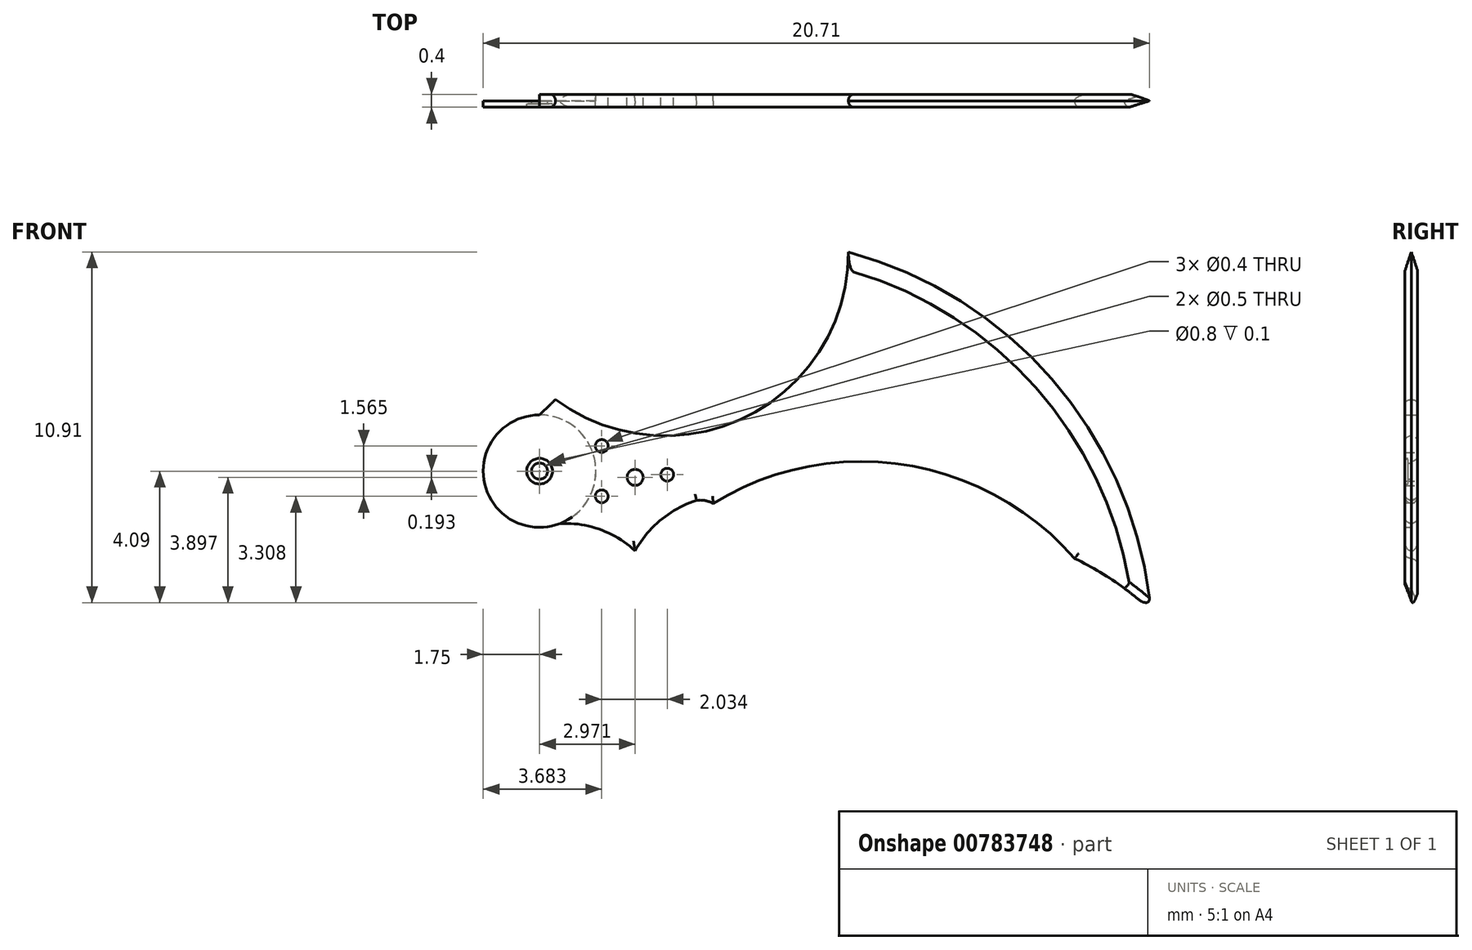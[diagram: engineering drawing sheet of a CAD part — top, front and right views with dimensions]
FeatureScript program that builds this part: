
annotation { "Feature Type Name" : "Feature", "Feature Type Description" : "" }
export const myFeature = defineFeature(function(context is Context, id is Id, definition is map)
    precondition{}
    {
        {
            var Q0;
            Q0=qCreatedBy(makeId("Front.planeOp"),FACE);
            var sketch = newSketch(context, id + "F0", { "sketchPlane" : qUnion([Q0])});
            skPoint(sketch, "E0", {"position": v(12.4, 0) * mm});
            skPoint(sketch, "E1", {"position": v(10, 3) * mm});
            skPoint(sketch, "E2", {"position": v(5.9, 7.4) * mm});
            skPoint(sketch, "E3", {"position": v(0.8, 6.7) * mm});
            skPoint(sketch, "E4", {"position": v(5, 9.8) * mm});
            skPoint(sketch, "E5", {"position": v(0, 11.5) * mm});
            skPoint(sketch, "E6", {"position": v(3.9, 18.3) * mm});
            skPoint(sketch, "E7", {"position": v(6.3, 6) * mm});
            skArc(sketch, "E8", {"start": v(2.97, 9.02) * mm, "mid": v(1.89, 9.68) * mm, "end": v(0.64, 9.87) * mm});
            skCircle(sketch, "E9", {"center": v(0, 11.5) * mm, "radius": 1.75 * mm});
            skArc(sketch, "E10", {"start": v(0.5, 13.73) * mm, "mid": v(6.46, 13.2) * mm, "end": v(9.6, 18.32) * mm});
            skArc(sketch, "E11", {"start": v(5.4, 10.5) * mm, "mid": v(5.14, 10.59) * mm, "end": v(4.88, 10.6) * mm});
            skArc(sketch, "E12", {"start": v(5.83, 10.75) * mm, "mid": v(4.17, 10.27) * mm, "end": v(2.97, 9.02) * mm});
            skArc(sketch, "E13", {"start": v(19, 7.18) * mm, "mid": v(16.04, 14.22) * mm, "end": v(9.6, 18.32) * mm});
            skArc(sketch, "E14", {"start": v(16.63, 8.78) * mm, "mid": v(11.33, 11.7) * mm, "end": v(5.4, 10.5) * mm});
            skArc(sketch, "E15.trimOffspring", {"start": v(19, 7.18) * mm, "mid": v(17.87, 8.07) * mm, "end": v(16.63, 8.78) * mm});
            skLineSegment(sketch, "E16", {"start": v(0, 13.25) * mm, "end": v(0.5, 13.73) * mm});
            skCircle(sketch, "E17", {"center": v(1.93, 12.28) * mm, "radius": 0.2 * mm});
            skLineSegment(sketch, "E18", {"start": v(0, 11.5) * mm, "end": v(5.59, 11.5) * mm, "construction": true});
            skCircle(sketch, "E19", {"center": v(2.97, 11.3) * mm, "radius": 0.25 * mm});
            skCircle(sketch, "E20", {"center": v(3.97, 11.39) * mm, "radius": 0.2 * mm});
            skCircle(sketch, "E21.MirrorC", {"center": v(1.93, 10.72) * mm, "radius": 0.2 * mm});
            skLineSegment(sketch, "E22", {"start": v(0, 15.23) * mm, "end": v(0, 8.3) * mm, "construction": true});
            skCircle(sketch, "E23", {"center": v(0, 11.5) * mm, "radius": 0.25 * mm});
            skCircle(sketch, "E24", {"center": v(0, 11.5) * mm, "radius": 0.4 * mm});
            skSolve(sketch);
        }
        {
            var Q0;
            {var subQ4=sQuery(id+"F0.wireOp",EDGE,"E8");Q0=makeQuery(id+"F0.imprint","IMPRINT",FACE,{"disambiguationData":[TD([[makeQuery(id+"F0.imprint","IMPRINT",EDGE,{"derivedFrom":subQ4}),-1.0]])]});}
            var Q1;
            {var subQ0=sQuery(id+"F0.wireOp",EDGE,"E14");var subQ1=sQuery(id+"F0.wireOp",EDGE,"E11");var subQ2=makeQuery(id+"F0.imprint","INTERSECT",VERTEX,{"derivedFrom":[subQ1,subQ0]});Q1=makeQuery(id+"F0.imprint","IMPRINT",FACE,{"disambiguationData":[TD([[makeQuery(id+"F0.imprint","IMPRINT",EDGE,{"disambiguationData":[TD([[subQ2,-1.0]])],"derivedFrom":subQ1}),-1.0]])]});}
            extrude(context, id + "F1", {"entities" : qUnion([Q0, Q1]), "endBound" : BoundingType.SYMMETRIC, "depth" : .4 * mm, "offsetDistance" : 25 * mm});
        }
        {
            var Q0;
            {var subQ0=sQuery(id+"F0.wireOp",EDGE,"E9");var subQ1=makeQuery(id+"F0.imprint","INTERSECT",VERTEX,{"derivedFrom":[sQuery(id+"F0.wireOp",EDGE,"E8"),subQ0]});Q0=makeQuery(id+"F0.imprint","IMPRINT",FACE,{"disambiguationData":[TD([[makeQuery(id+"F0.imprint","IMPRINT",EDGE,{"disambiguationData":[TD([[subQ1,1.0]])],"derivedFrom":subQ0}),1.0]])]});}
            extrude(context, id + "F2", {"entities" : qUnion([Q0]), "operationType" : NewBodyOperationType.ADD, "depth" : .2 * mm, "offsetDistance" : 25 * mm});
        }
        {
            var Q0;
            Q0=makeQuery(id+"F1.opExtrude","CAP_EDGE",EDGE,{"disambiguationData":[OSD([sQuery(id+"F0.wireOp",EDGE,"E13")])],"isStart":false});
            var Q1;
            Q1=makeQuery(id+"F1.opExtrude","CAP_EDGE",EDGE,{"disambiguationData":[OSD([sQuery(id+"F0.wireOp",EDGE,"E13")])],"isStart":true});
            chamfer(context, id + "F3", {"entities" : qUnion([Q0, Q1]), "chamferType" : ChamferType.OFFSET_ANGLE, "width" : .55 * mm, "oppositeDirection" : false, "angle" : 20 * degree, "tangentPropagation" : true});
        }
        {
            var Q0;
            Q0=makeQuery(id+"F1.opExtrude","CAP_EDGE",EDGE,{"disambiguationData":[OSD([sQuery(id+"F0.wireOp",EDGE,"E10")])],"isStart":false});
            var Q1;
            Q1=makeQuery(id+"F1.opExtrude","CAP_EDGE",EDGE,{"disambiguationData":[OSD([sQuery(id+"F0.wireOp",EDGE,"E14")])],"isStart":false});
            var Q2;
            {var subQ0=sQuery(id+"F0.wireOp",EDGE,"E12");Q2=makeQuery(id+"F1.opExtrude","CAP_EDGE",EDGE,{"disambiguationData":[OSD([subQ0]),TDD([makeQuery(id+"F0.imprint","IMPRINT",EDGE,{"disambiguationData":[TD([[makeQuery(id+"F0.imprint","INTERSECT",VERTEX,{"derivedFrom":[subQ0,sQuery(id+"F0.wireOp",EDGE,"E14")]}),-1.0]])],"derivedFrom":subQ0})])],"isStart":false});}
            var Q3;
            {var subQ0=sQuery(id+"F0.wireOp",EDGE,"E12");Q3=makeQuery(id+"F1.opExtrude","CAP_EDGE",EDGE,{"disambiguationData":[OSD([subQ0]),TDD([makeQuery(id+"F0.imprint","IMPRINT",EDGE,{"disambiguationData":[TD([[makeQuery(id+"F0.imprint","INTERSECT",VERTEX,{"derivedFrom":[sQuery(id+"F0.wireOp",EDGE,"E8"),subQ0]}),1.0]])],"derivedFrom":subQ0})])],"isStart":false});}
            var Q4;
            Q4=makeQuery(id+"F1.opExtrude","CAP_EDGE",EDGE,{"disambiguationData":[OSD([sQuery(id+"F0.wireOp",EDGE,"E11")])],"isStart":false});
            var Q5;
            {var subQ0=sQuery(id+"F0.wireOp",EDGE,"E12");Q5=makeQuery(id+"F1.opExtrude","CAP_EDGE",EDGE,{"disambiguationData":[OSD([subQ0]),TDD([makeQuery(id+"F0.imprint","IMPRINT",EDGE,{"disambiguationData":[TD([[makeQuery(id+"F0.imprint","INTERSECT",VERTEX,{"derivedFrom":[sQuery(id+"F0.wireOp",EDGE,"E8"),subQ0]}),1.0]])],"derivedFrom":subQ0})])],"isStart":true});}
            var Q6;
            {var subQ0=sQuery(id+"F0.wireOp",EDGE,"E12");Q6=makeQuery(id+"F1.opExtrude","CAP_EDGE",EDGE,{"disambiguationData":[OSD([subQ0]),TDD([makeQuery(id+"F0.imprint","IMPRINT",EDGE,{"disambiguationData":[TD([[makeQuery(id+"F0.imprint","INTERSECT",VERTEX,{"derivedFrom":[subQ0,sQuery(id+"F0.wireOp",EDGE,"E14")]}),-1.0]])],"derivedFrom":subQ0})])],"isStart":true});}
            var Q7;
            Q7=makeQuery(id+"F1.opExtrude","CAP_EDGE",EDGE,{"disambiguationData":[OSD([sQuery(id+"F0.wireOp",EDGE,"E11")])],"isStart":true});
            var Q8;
            Q8=makeQuery(id+"F1.opExtrude","CAP_EDGE",EDGE,{"disambiguationData":[OSD([sQuery(id+"F0.wireOp",EDGE,"E14")])],"isStart":true});
            var Q9;
            Q9=makeQuery(id+"F1.opExtrude","CAP_EDGE",EDGE,{"disambiguationData":[OSD([sQuery(id+"F0.wireOp",EDGE,"E8")])],"isStart":true});
            var Q10;
            Q10=makeQuery(id+"F1.opExtrude","CAP_EDGE",EDGE,{"disambiguationData":[OSD([sQuery(id+"F0.wireOp",EDGE,"E8")])],"isStart":false});
            var Q11;
            Q11=makeQuery(id+"F1.opExtrude","CAP_EDGE",EDGE,{"disambiguationData":[OSD([sQuery(id+"F0.wireOp",EDGE,"E10")])],"isStart":true});
            var Q12;
            Q12=makeQuery(id+"F1.opExtrude","CAP_EDGE",EDGE,{"disambiguationData":[OSD([sQuery(id+"F0.wireOp",EDGE,"E15.trimOffspring")])],"isStart":false});
            var Q13;
            Q13=makeQuery(id+"F3.opChamfer","BLEND_EDGE",EDGE,{"blendedFrom":[makeQuery(id+"F1.opExtrude","CAP_EDGE",EDGE,{"disambiguationData":[OSD([sQuery(id+"F0.wireOp",EDGE,"E13")])],"isStart":false}),makeQuery(id+"F1.opExtrude","SWEPT_FACE",FACE,{"disambiguationData":[OSD([sQuery(id+"F0.wireOp",EDGE,"E15.trimOffspring")])]})],"blendedInto":[makeQuery(id+"F1.opExtrude","SWEPT_FACE",FACE,{"disambiguationData":[OSD([sQuery(id+"F0.wireOp",EDGE,"E15.trimOffspring")])]})]});
            fillet(context, id + "F4", {"entities" : qUnion([Q0, Q1, Q2, Q3, Q4, Q5, Q6, Q7, Q8, Q9, Q10, Q11, Q12, Q13]), "radius" : .2 * mm, "tangentPropagation" : true, "allowEdgeOverflow" : false});
        }
        {
            var Q0;
            Q0=makeQuery(id+"F0.imprint","IMPRINT",FACE,{"disambiguationData":[TD([[makeQuery(id+"F0.imprint","IMPRINT",EDGE,{"derivedFrom":sQuery(id+"F0.wireOp",EDGE,"E23")}),-1.0]])]});
            extrude(context, id + "F5", {"entities" : qUnion([Q0]), "operationType" : NewBodyOperationType.REMOVE, "oppositeDirection" : true, "depth" : .5 * mm, "offsetDistance" : 25 * mm});
        }
        {
            var Q0;
            Q0=makeQuery(id+"F0.imprint","IMPRINT",FACE,{"disambiguationData":[TD([[makeQuery(id+"F0.imprint","IMPRINT",EDGE,{"derivedFrom":sQuery(id+"F0.wireOp",EDGE,"E23")}),-1.0]])]});
            extrude(context, id + "F6", {"entities" : qUnion([Q0]), "operationType" : NewBodyOperationType.ADD, "depth" : .1 * mm, "offsetDistance" : 25 * mm});
        }
    });
